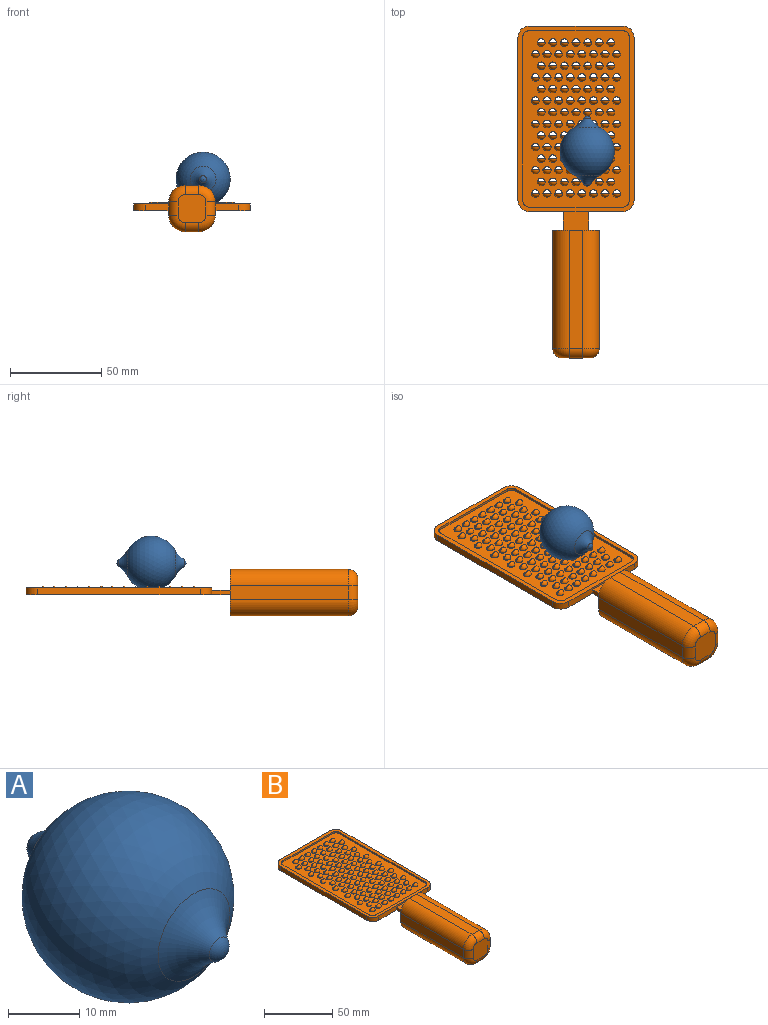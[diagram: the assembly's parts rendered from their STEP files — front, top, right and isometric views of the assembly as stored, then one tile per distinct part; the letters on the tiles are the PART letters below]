
ASSEMBLY  parts=2 mates=1
PART A: 5 faces, bbox 29.7x49.9x29.7 mm
  f0: sphere r=14.84mm, area 2431.8mm2, adj f1,f4
  f1: torus R=13.59mm, axis (0,-1,0), area 195.4mm2, adj f0,f2
  f2: sphere r=2.29mm, area 15.1mm2, adj f1
  f3: sphere r=2.29mm, area 15.1mm2, adj f4
  f4: torus R=13.59mm, axis (0,-1,0), area 195.4mm2, adj f0,f3
PART B: 462 faces, bbox 63.5x181.6x25.4 mm
  f0: plane 96.55x58.45mm, normal (0,0,1), area 4213mm2, adj f11,f12,f13,f14,f15,f16,f17,f18
  f1: plane 50.8x3.81mm, normal (0,-1,0), area 158.1mm2, adj f2,f4,f5,f10,f124,f125,f126
  f2: plane 101.6x63.5mm, normal (0,0,1), area 790.7mm2, adj f1,f3,f4,f5,f6,f7,f8,f9
  f3: plane 88.9x3.81mm, normal (-1,0,0), area 338.7mm2, adj f2,f4,f9,f10
  f4: cylinder r=6.35mm len=6.35mm, axis (0,0,-1), area 38mm2, adj f1,f2,f3,f10
  f5: cylinder r=6.35mm len=6.35mm, axis (0,0,-1), area 38mm2, adj f1,f2,f6,f10
  f6: plane 88.9x3.81mm, normal (1,0,0), area 338.7mm2, adj f2,f5,f7,f10
  f7: cylinder r=6.35mm len=6.35mm, axis (0,0,-1), area 38mm2, adj f2,f6,f8,f10
  f8: plane 50.8x3.81mm, normal (0,1,0), area 193.5mm2, adj f2,f7,f9,f10
  f9: cylinder r=6.35mm len=6.35mm, axis (0,0,-1), area 38mm2, adj f2,f3,f8,f10
  f10: plane 111.76x63.5mm, normal (0,0,-1), area 5361.8mm2, adj f1,f3,f4,f5,f6,f7,f8,f9
  f11: plane 88.9x1.27mm, normal (1,0,0), area 112.9mm2, adj f0,f2,f12,f18
  f12: cylinder r=3.81mm len=3.81mm, axis (0,0,-1), area 7.6mm2, adj f0,f2,f11,f13
  f13: plane 50.8x1.27mm, normal (0,1,0), area 64.5mm2, adj f0,f2,f12,f14
  f14: cylinder r=3.81mm len=3.81mm, axis (0,0,-1), area 7.6mm2, adj f0,f2,f13,f15
  f15: plane 88.9x1.27mm, normal (-1,0,0), area 112.9mm2, adj f0,f2,f14,f16
  f16: cylinder r=3.81mm len=3.81mm, axis (0,0,-1), area 7.6mm2, adj f0,f2,f15,f17
  f17: plane 50.8x1.27mm, normal (0,-1,0), area 64.5mm2, adj f0,f2,f16,f18
  f18: cylinder r=3.81mm len=3.81mm, axis (0,0,-1), area 7.6mm2, adj f0,f2,f11,f17
  f19: cylinder r=1.91mm len=3.81mm, axis (0,0,1), area 30.4mm2, adj f0,f10,f166
  f20: cylinder r=1.91mm len=3.81mm, axis (0,0,1), area 30.4mm2, adj f0,f10,f430
  f21: cylinder r=1.91mm len=3.81mm, axis (0,0,1), area 30.4mm2, adj f0,f10,f206
  f22: cylinder r=1.91mm len=3.81mm, axis (0,0,1), area 30.4mm2, adj f0,f10,f274,f275,f278
  f23: cylinder r=1.91mm len=3.81mm, axis (0,0,1), area 30.4mm2, adj f0,f10,f297
  f24: cylinder r=1.91mm len=3.81mm, axis (0,0,1), area 30.4mm2, adj f0,f10,f385
  f25: cylinder r=1.91mm len=3.81mm, axis (0,0,1), area 30.4mm2, adj f0,f10,f339
  f26: cylinder r=1.91mm len=3.81mm, axis (0,0,1), area 30.4mm2, adj f0,f10,f294
  f27: cylinder r=1.91mm len=3.81mm, axis (0,0,1), area 30.4mm2, adj f0,f10,f247
  f28: cylinder r=1.91mm len=3.81mm, axis (0,0,1), area 30.4mm2, adj f0,f10,f391
  f29: cylinder r=1.91mm len=3.81mm, axis (0,0,1), area 30.4mm2, adj f0,f10,f345
  f30: cylinder r=1.91mm len=3.81mm, axis (0,0,1), area 30.4mm2, adj f0,f10,f300
  f31: cylinder r=1.91mm len=3.81mm, axis (0,0,1), area 30.4mm2, adj f0,f10,f268
  f32: cylinder r=1.91mm len=3.81mm, axis (0,0,1), area 30.4mm2, adj f0,f10,f342
  f33: cylinder r=1.91mm len=3.81mm, axis (0,0,1), area 30.4mm2, adj f0,f10,f388
  f34: cylinder r=1.91mm len=3.81mm, axis (0,0,1), area 30.4mm2, adj f0,f10,f433
  f35: cylinder r=1.91mm len=3.81mm, axis (0,0,1), area 30.4mm2, adj f0,f10,f208
  f36: cylinder r=1.91mm len=3.81mm, axis (0,0,1), area 30.4mm2, adj f0,f10,f379
  f37: cylinder r=1.91mm len=3.81mm, axis (0,0,1), area 30.4mm2, adj f0,f10,f333
  f38: cylinder r=1.91mm len=3.81mm, axis (0,0,1), area 30.4mm2, adj f0,f10,f288
  f39: cylinder r=1.91mm len=3.81mm, axis (0,0,1), area 30.4mm2, adj f0,f10,f241
  f40: cylinder r=1.91mm len=3.81mm, axis (0,0,1), area 30.4mm2, adj f0,f10,f331
  f41: cylinder r=1.91mm len=3.81mm, axis (0,0,1), area 30.4mm2, adj f0,f10,f376
  f42: cylinder r=1.91mm len=3.81mm, axis (0,0,1), area 30.4mm2, adj f0,f10,f421
  f43: cylinder r=1.91mm len=3.81mm, axis (0,0,1), area 30.4mm2, adj f0,f10,f196
  f44: cylinder r=1.91mm len=3.81mm, axis (0,0,1), area 30.4mm2, adj f0,f10,f336
  f45: cylinder r=1.91mm len=3.81mm, axis (0,0,1), area 30.4mm2, adj f0,f10,f382
  f46: cylinder r=1.91mm len=3.81mm, axis (0,0,1), area 30.4mm2, adj f0,f10,f427
  f47: cylinder r=1.91mm len=3.81mm, axis (0,0,1), area 30.4mm2, adj f0,f10,f203
  f48: cylinder r=1.91mm len=3.81mm, axis (0,0,1), area 30.4mm2, adj f0,f10,f424
  f49: cylinder r=1.91mm len=3.81mm, axis (0,0,1), area 30.4mm2, adj f0,f10,f199
  f50: cylinder r=1.91mm len=3.81mm, axis (0,0,1), area 30.4mm2, adj f0,f10,f244
  f51: cylinder r=1.91mm len=3.81mm, axis (0,0,1), area 30.4mm2, adj f0,f10,f291
  f52: cylinder r=1.91mm len=3.81mm, axis (0,0,1), area 30.4mm2, adj f0,f10,f154
  f53: cylinder r=1.91mm len=3.81mm, axis (0,0,1), area 30.4mm2, adj f0,f10,f160
  f54: cylinder r=1.91mm len=3.81mm, axis (0,0,1), area 30.4mm2, adj f0,f10,f163
  f55: cylinder r=1.91mm len=3.81mm, axis (0,0,1), area 30.4mm2, adj f0,f10,f157
  f56: cylinder r=1.91mm len=3.81mm, axis (0,0,1), area 30.4mm2, adj f0,f10,f436
  f57: cylinder r=1.91mm len=3.81mm, axis (0,0,1), area 30.4mm2, adj f0,f10,f145
  f58: cylinder r=1.91mm len=3.81mm, axis (0,0,1), area 30.4mm2, adj f0,f10,f148
  f59: cylinder r=1.91mm len=3.81mm, axis (0,0,1), area 30.4mm2, adj f0,f10,f151
  f60: cylinder r=1.91mm len=3.81mm, axis (0,0,1), area 30.4mm2, adj f0,f10,f309
  f61: cylinder r=1.91mm len=3.81mm, axis (0,0,1), area 30.4mm2, adj f0,f10,f355
  f62: cylinder r=1.91mm len=3.81mm, axis (0,0,1), area 30.4mm2, adj f0,f10,f400
  f63: cylinder r=1.91mm len=3.81mm, axis (0,0,1), area 30.4mm2, adj f0,f10,f445
  f64: cylinder r=1.91mm len=3.81mm, axis (0,0,1), area 30.4mm2, adj f0,f10,f175
  f65: cylinder r=1.91mm len=3.81mm, axis (0,0,1), area 30.4mm2, adj f0,f10,f220
  f66: cylinder r=1.91mm len=3.81mm, axis (0,0,1), area 30.4mm2, adj f0,f10,f259
  f67: cylinder r=1.91mm len=3.81mm, axis (0,0,1), area 30.4mm2, adj f0,f10,f312
  f68: cylinder r=1.91mm len=3.81mm, axis (0,0,1), area 30.4mm2, adj f0,f10,f361
  f69: cylinder r=1.91mm len=3.81mm, axis (0,0,1), area 30.4mm2, adj f0,f10,f315
  f70: cylinder r=1.91mm len=3.81mm, axis (0,0,1), area 30.4mm2, adj f0,f10,f262
  f71: cylinder r=1.91mm len=3.81mm, axis (0,0,1), area 30.4mm2, adj f0,f10,f223
  f72: cylinder r=1.91mm len=3.81mm, axis (0,0,1), area 30.4mm2, adj f0,f10,f358
  f73: cylinder r=1.91mm len=3.81mm, axis (0,0,1), area 30.4mm2, adj f0,f10,f403
  f74: cylinder r=1.91mm len=3.81mm, axis (0,0,1), area 30.4mm2, adj f0,f10,f448
  f75: cylinder r=1.91mm len=3.81mm, axis (0,0,1), area 30.4mm2, adj f0,f10,f178
  f76: cylinder r=1.91mm len=3.81mm, axis (0,0,1), area 30.4mm2, adj f0,f10,f214
  f77: cylinder r=1.91mm len=3.81mm, axis (0,0,1), area 30.4mm2, adj f0,f10,f169
  f78: cylinder r=1.91mm len=3.81mm, axis (0,0,1), area 30.4mm2, adj f0,f10,f439
  f79: cylinder r=1.91mm len=3.81mm, axis (0,0,1), area 30.4mm2, adj f0,f10,f394
  f80: cylinder r=1.91mm len=3.81mm, axis (0,0,1), area 30.4mm2, adj f0,f10,f348
  f81: cylinder r=1.91mm len=3.81mm, axis (0,0,1), area 30.4mm2, adj f0,f10,f303
  f82: cylinder r=1.91mm len=3.81mm, axis (0,0,1), area 30.4mm2, adj f0,f10,f250
  f83: cylinder r=1.91mm len=3.81mm, axis (0,0,1), area 30.4mm2, adj f0,f10,f212
  f84: cylinder r=1.91mm len=3.81mm, axis (0,0,1), area 30.4mm2, adj f0,f10,f442
  f85: cylinder r=1.91mm len=3.81mm, axis (0,0,1), area 30.4mm2, adj f0,f10,f172
  f86: cylinder r=1.91mm len=3.81mm, axis (0,0,1), area 30.4mm2, adj f0,f10,f217
  f87: cylinder r=1.91mm len=3.81mm, axis (0,0,1), area 30.4mm2, adj f0,f10,f256
  f88: cylinder r=1.91mm len=3.81mm, axis (0,0,1), area 30.4mm2, adj f0,f10,f397
  f89: cylinder r=1.91mm len=3.81mm, axis (0,0,1), area 30.4mm2, adj f0,f10,f352
  f90: cylinder r=1.91mm len=3.81mm, axis (0,0,1), area 30.4mm2, adj f0,f10,f306
  f91: cylinder r=1.91mm len=3.81mm, axis (0,0,1), area 30.4mm2, adj f0,f10,f253
  f92: cylinder r=1.91mm len=3.81mm, axis (0,0,1), area 30.4mm2, adj f0,f10,f370
  f93: cylinder r=1.91mm len=3.81mm, axis (0,0,1), area 30.4mm2, adj f0,f10,f415
  f94: cylinder r=1.91mm len=3.81mm, axis (0,0,1), area 30.4mm2, adj f0,f10,f460
  f95: cylinder r=1.91mm len=3.81mm, axis (0,0,1), area 30.4mm2, adj f0,f10,f190
  f96: cylinder r=1.91mm len=3.81mm, axis (0,0,1), area 30.4mm2, adj f0,f10,f324
  f97: cylinder r=1.91mm len=3.81mm, axis (0,0,1), area 30.4mm2, adj f0,f10,f279
  f98: cylinder r=1.91mm len=3.81mm, axis (0,0,1), area 30.4mm2, adj f0,f10,f233
  f99: cylinder r=1.91mm len=3.81mm, axis (0,0,1), area 30.4mm2, adj f0,f10,f187
  f100: cylinder r=1.91mm len=3.81mm, axis (0,0,1), area 30.4mm2, adj f0,f10,f418
  f101: cylinder r=1.91mm len=3.81mm, axis (0,0,1), area 30.4mm2, adj f0,f10,f193
  f102: cylinder r=1.91mm len=3.81mm, axis (0,0,1), area 30.4mm2, adj f0,f10,f238
  f103: cylinder r=1.91mm len=3.81mm, axis (0,0,1), area 30.4mm2, adj f0,f10,f285
  f104: cylinder r=1.91mm len=3.81mm, axis (0,0,1), area 30.4mm2, adj f0,f10,f372
  f105: cylinder r=1.91mm len=3.81mm, axis (0,0,1), area 30.4mm2, adj f0,f10,f327
  f106: cylinder r=1.91mm len=3.81mm, axis (0,0,1), area 30.4mm2, adj f0,f10,f282
  f107: cylinder r=1.91mm len=3.81mm, axis (0,0,1), area 30.4mm2, adj f0,f10,f235
  f108: cylinder r=1.91mm len=3.81mm, axis (0,0,1), area 30.4mm2, adj f0,f10,f409
  f109: cylinder r=1.91mm len=3.81mm, axis (0,0,1), area 30.4mm2, adj f0,f10,f364
  f110: cylinder r=1.91mm len=3.81mm, axis (0,0,1), area 30.4mm2, adj f0,f10,f320
  f111: cylinder r=1.91mm len=3.81mm, axis (0,0,1), area 30.4mm2, adj f0,f10,f265
  f112: cylinder r=1.91mm len=3.81mm, axis (0,0,1), area 30.4mm2, adj f0,f10,f226
  f113: cylinder r=1.91mm len=3.81mm, axis (0,0,1), area 30.4mm2, adj f0,f10,f181
  f114: cylinder r=1.91mm len=3.81mm, axis (0,0,1), area 30.4mm2, adj f0,f10,f451
  f115: cylinder r=1.91mm len=3.81mm, axis (0,0,1), area 30.4mm2, adj f0,f10,f406
  f116: cylinder r=1.91mm len=3.81mm, axis (0,0,1), area 30.4mm2, adj f0,f10,f457
  f117: cylinder r=1.91mm len=3.81mm, axis (0,0,1), area 30.4mm2, adj f0,f10,f412
  f118: cylinder r=1.91mm len=3.81mm, axis (0,0,1), area 30.4mm2, adj f0,f10,f367
  f119: cylinder r=1.91mm len=3.81mm, axis (0,0,1), area 30.4mm2, adj f0,f10,f321
  f120: cylinder r=1.91mm len=3.81mm, axis (0,0,1), area 30.4mm2, adj f0,f10,f454
  f121: cylinder r=1.91mm len=3.81mm, axis (0,0,1), area 30.4mm2, adj f0,f10,f184
  f122: cylinder r=1.91mm len=3.81mm, axis (0,0,1), area 30.4mm2, adj f0,f10,f229
  f123: cylinder r=1.91mm len=3.81mm, axis (0,0,1), area 30.4mm2, adj f0,f10,f271
  f124: plane 10.16x2.54mm, normal (1,0,0), area 25.8mm2, adj f1,f10,f125,f136
  f125: plane 13.97x10.16mm, normal (0,0,1), area 141.9mm2, adj f1,f124,f126,f136
  f126: plane 10.16x2.54mm, normal (-1,0,0), area 25.8mm2, adj f1,f10,f125,f136
  f127: plane 64.77x7.62mm, normal (-1,0,0), area 493.5mm2, adj f128,f134,f136,f141
  f128: cylinder r=8.89mm len=64.77mm, axis (0,1,0), area 904.5mm2, adj f127,f129,f136,f139
  f129: plane 64.77x7.62mm, normal (0,0,-1), area 493.5mm2, adj f128,f130,f136,f137
  f130: cylinder r=8.89mm len=64.77mm, axis (0,1,0), area 904.5mm2, adj f129,f131,f136,f138
  f131: plane 64.77x7.62mm, normal (1,0,0), area 493.5mm2, adj f130,f132,f136,f140
  f132: cylinder r=8.89mm len=64.77mm, axis (0,1,0), area 904.5mm2, adj f131,f133,f136,f142
  f133: plane 64.77x7.62mm, normal (0,0,1), area 493.5mm2, adj f132,f134,f136,f144
  f134: cylinder r=8.89mm len=64.77mm, axis (0,1,0), area 904.5mm2, adj f127,f133,f136,f143
  f135: plane 15.24x15.24mm, normal (0,-1,0), area 219.8mm2, adj f137,f138,f139,f140,f141,f142,f143,f144
  f136: plane 25.4x25.4mm, normal (0,1,0), area 541.8mm2, adj f10,f124,f125,f126,f127,f128,f129,f130
  f137: cylinder r=5.08mm len=7.62mm, axis (-1,0,0), area 60.8mm2, adj f129,f135,f138,f139
  f138: torus R=3.81mm, axis (0,-1,0), area 88.3mm2, adj f130,f135,f137,f140
  f139: torus R=3.81mm, axis (0,-1,0), area 88.3mm2, adj f128,f135,f137,f141
  f140: cylinder r=5.08mm len=7.62mm, axis (0,0,-1), area 60.8mm2, adj f131,f135,f138,f142
  f141: cylinder r=5.08mm len=7.62mm, axis (0,0,1), area 60.8mm2, adj f127,f135,f139,f143
  f142: torus R=3.81mm, axis (0,-1,0), area 88.3mm2, adj f132,f135,f140,f144
  f143: torus R=3.81mm, axis (0,-1,0), area 88.3mm2, adj f134,f135,f141,f144
  f144: cylinder r=5.08mm len=7.62mm, axis (1,0,0), area 60.8mm2, adj f133,f135,f142,f143
  f145: sphere r=1.91mm, area 11.4mm2, adj f57,f146
  f146: plane 4.45x2.22mm, normal (0,1,0), area 2.1mm2, adj f0,f145,f147
  f147: sphere r=2.22mm, area 15.5mm2, adj f0,f146
  f148: sphere r=1.91mm, area 11.4mm2, adj f58,f149
  f149: plane 4.45x2.22mm, normal (0,1,0), area 2.1mm2, adj f0,f148,f150
  f150: sphere r=2.22mm, area 15.5mm2, adj f0,f149
  f151: sphere r=1.91mm, area 11.4mm2, adj f59,f152
  f152: plane 4.45x2.22mm, normal (0,1,0), area 2.1mm2, adj f0,f151,f153
  f153: sphere r=2.22mm, area 15.5mm2, adj f0,f152
  f154: sphere r=1.91mm, area 11.4mm2, adj f52,f155
  f155: plane 4.45x2.22mm, normal (0,1,0), area 2.1mm2, adj f0,f154,f156
  f156: sphere r=2.22mm, area 15.5mm2, adj f0,f155
  f157: sphere r=1.91mm, area 11.4mm2, adj f55,f158
  f158: plane 4.45x2.22mm, normal (0,1,0), area 2.1mm2, adj f0,f157,f159
  f159: sphere r=2.22mm, area 15.5mm2, adj f0,f158
  f160: sphere r=1.91mm, area 11.4mm2, adj f53,f161
  f161: plane 4.45x2.22mm, normal (0,1,0), area 2.1mm2, adj f0,f160,f162
  f162: sphere r=2.22mm, area 15.5mm2, adj f0,f161
  f163: sphere r=1.91mm, area 11.4mm2, adj f54,f164
  f164: plane 4.45x2.22mm, normal (0,1,0), area 2.1mm2, adj f0,f163,f165
  f165: sphere r=2.22mm, area 15.5mm2, adj f0,f164
  f166: sphere r=1.91mm, area 11.4mm2, adj f19,f167
  f167: plane 4.45x2.22mm, normal (0,1,0), area 2.1mm2, adj f0,f166,f168
  f168: sphere r=2.22mm, area 15.5mm2, adj f0,f167
  f169: sphere r=1.91mm, area 11.4mm2, adj f77,f170
  f170: plane 4.45x2.22mm, normal (0,1,0), area 2.1mm2, adj f0,f169,f171
  f171: sphere r=2.22mm, area 15.5mm2, adj f0,f170
  f172: sphere r=1.91mm, area 11.4mm2, adj f85,f173
  f173: plane 4.45x2.22mm, normal (0,1,0), area 2.1mm2, adj f0,f172,f174
  f174: sphere r=2.22mm, area 15.5mm2, adj f0,f173
  f175: sphere r=1.91mm, area 11.4mm2, adj f64,f176
  f176: plane 4.45x2.22mm, normal (0,1,0), area 2.1mm2, adj f0,f175,f177
  f177: sphere r=2.22mm, area 15.5mm2, adj f0,f176
  f178: sphere r=1.91mm, area 11.4mm2, adj f75,f179
  f179: plane 4.45x2.22mm, normal (0,1,0), area 2.1mm2, adj f0,f178,f180
  f180: sphere r=2.22mm, area 15.5mm2, adj f0,f179
  f181: sphere r=1.91mm, area 11.4mm2, adj f113,f182
  f182: plane 4.45x2.22mm, normal (0,1,0), area 2.1mm2, adj f0,f181,f183
  f183: sphere r=2.22mm, area 15.5mm2, adj f0,f182
  f184: sphere r=1.91mm, area 11.4mm2, adj f121,f185
  f185: plane 4.45x2.22mm, normal (0,1,0), area 2.1mm2, adj f0,f184,f186
  f186: sphere r=2.22mm, area 15.5mm2, adj f0,f185
  f187: sphere r=1.91mm, area 11.4mm2, adj f99,f188
  f188: plane 4.45x2.22mm, normal (0,1,0), area 2.1mm2, adj f0,f187,f189
  f189: sphere r=2.22mm, area 15.5mm2, adj f0,f188
  f190: sphere r=1.91mm, area 11.4mm2, adj f95,f191
  f191: plane 4.45x2.22mm, normal (0,1,0), area 2.1mm2, adj f0,f190,f192
  f192: sphere r=2.22mm, area 15.5mm2, adj f0,f191
  f193: sphere r=1.91mm, area 11.4mm2, adj f101,f194
  f194: plane 4.45x2.22mm, normal (0,1,0), area 2.1mm2, adj f0,f193,f195
  f195: sphere r=2.22mm, area 15.5mm2, adj f0,f194
  f196: sphere r=1.91mm, area 11.4mm2, adj f43,f198
  f197: sphere r=2.22mm, area 15.5mm2, adj f0,f198
  f198: plane 4.45x2.22mm, normal (0,1,0), area 2.1mm2, adj f0,f196,f197
  f199: sphere r=1.91mm, area 11.4mm2, adj f49,f201
  f200: sphere r=2.22mm, area 15.5mm2, adj f0,f201
  f201: plane 4.45x2.22mm, normal (0,1,0), area 2.1mm2, adj f0,f199,f200
  f202: plane 4.45x2.22mm, normal (0,1,0), area 2.1mm2, adj f0,f203,f204
  f203: sphere r=1.91mm, area 11.4mm2, adj f47,f202
  f204: sphere r=2.22mm, area 15.5mm2, adj f0,f202
  f205: plane 4.45x2.22mm, normal (0,1,0), area 2.1mm2, adj f0,f206,f207
  f206: sphere r=1.91mm, area 11.4mm2, adj f21,f205
  f207: sphere r=2.22mm, area 15.5mm2, adj f0,f205
  f208: sphere r=1.91mm, area 11.4mm2, adj f35,f210
  f209: sphere r=2.22mm, area 15.5mm2, adj f0,f210
  f210: plane 4.45x2.22mm, normal (0,1,0), area 2.1mm2, adj f0,f208,f209
  f211: plane 4.45x2.22mm, normal (0,1,0), area 2.1mm2, adj f0,f212,f213
  f212: sphere r=1.91mm, area 11.4mm2, adj f83,f211
  f213: sphere r=2.22mm, area 15.5mm2, adj f0,f211
  f214: sphere r=1.91mm, area 11.4mm2, adj f76,f216
  f215: sphere r=2.22mm, area 15.5mm2, adj f0,f216
  f216: plane 4.45x2.22mm, normal (0,1,0), area 2.1mm2, adj f0,f214,f215
  f217: sphere r=1.91mm, area 11.4mm2, adj f86,f219
  f218: sphere r=2.22mm, area 15.5mm2, adj f0,f219
  f219: plane 4.45x2.22mm, normal (0,1,0), area 2.1mm2, adj f0,f217,f218
  f220: sphere r=1.91mm, area 11.4mm2, adj f65,f222
  f221: sphere r=2.22mm, area 15.5mm2, adj f0,f222
  f222: plane 4.45x2.22mm, normal (0,1,0), area 2.1mm2, adj f0,f220,f221
  f223: sphere r=1.91mm, area 11.4mm2, adj f71,f225
  f224: sphere r=2.22mm, area 15.5mm2, adj f0,f225
  f225: plane 4.45x2.22mm, normal (0,1,0), area 2.1mm2, adj f0,f223,f224
  f226: sphere r=1.91mm, area 11.4mm2, adj f112,f228
  f227: sphere r=2.22mm, area 15.5mm2, adj f0,f228
  f228: plane 4.45x2.22mm, normal (0,1,0), area 2.1mm2, adj f0,f226,f227
  f229: sphere r=1.91mm, area 11.4mm2, adj f122,f231
  f230: sphere r=2.22mm, area 15.5mm2, adj f0,f231
  f231: plane 4.45x2.22mm, normal (0,1,0), area 2.1mm2, adj f0,f229,f230
  f232: plane 4.45x2.22mm, normal (0,1,0), area 2.1mm2, adj f0,f233,f234
  f233: sphere r=1.91mm, area 11.4mm2, adj f98,f232
  f234: sphere r=2.22mm, area 15.5mm2, adj f0,f232
  f235: sphere r=1.91mm, area 11.4mm2, adj f107,f237
  f236: sphere r=2.22mm, area 15.5mm2, adj f0,f237
  f237: plane 4.45x2.22mm, normal (0,1,0), area 2.1mm2, adj f0,f235,f236
  f238: sphere r=1.91mm, area 11.4mm2, adj f102,f240
  f239: sphere r=2.22mm, area 15.5mm2, adj f0,f240
  f240: plane 4.45x2.22mm, normal (0,1,0), area 2.1mm2, adj f0,f238,f239
  f241: sphere r=1.91mm, area 11.4mm2, adj f39,f243
  f242: sphere r=2.22mm, area 15.5mm2, adj f0,f243
  f243: plane 4.45x2.22mm, normal (0,1,0), area 2.1mm2, adj f0,f241,f242
  f244: sphere r=1.91mm, area 11.4mm2, adj f50,f246
  f245: sphere r=2.22mm, area 15.5mm2, adj f0,f246
  f246: plane 4.45x2.22mm, normal (0,1,0), area 2.1mm2, adj f0,f244,f245
  f247: sphere r=1.91mm, area 11.4mm2, adj f27,f249
  f248: sphere r=2.22mm, area 15.5mm2, adj f0,f249
  f249: plane 4.45x2.22mm, normal (0,1,0), area 2.1mm2, adj f0,f247,f248
  f250: sphere r=1.91mm, area 11.4mm2, adj f82,f252
  f251: sphere r=2.22mm, area 15.5mm2, adj f0,f252
  f252: plane 4.45x2.22mm, normal (0,1,0), area 2.1mm2, adj f0,f250,f251
  f253: sphere r=1.91mm, area 11.4mm2, adj f91,f255
  f254: sphere r=2.22mm, area 15.5mm2, adj f0,f255
  f255: plane 4.45x2.22mm, normal (0,1,0), area 2.1mm2, adj f0,f253,f254
  f256: sphere r=1.91mm, area 11.4mm2, adj f87,f258
  f257: sphere r=2.22mm, area 15.5mm2, adj f0,f258
  f258: plane 4.45x2.22mm, normal (0,1,0), area 2.1mm2, adj f0,f256,f257
  f259: sphere r=1.91mm, area 11.4mm2, adj f66,f261
  f260: sphere r=2.22mm, area 15.5mm2, adj f0,f261
  f261: plane 4.45x2.22mm, normal (0,1,0), area 2.1mm2, adj f0,f259,f260
  f262: sphere r=1.91mm, area 11.4mm2, adj f70,f264
  f263: sphere r=2.22mm, area 15.5mm2, adj f0,f264
  f264: plane 4.45x2.22mm, normal (0,1,0), area 2.1mm2, adj f0,f262,f263
  f265: sphere r=1.91mm, area 11.4mm2, adj f111,f267
  f266: sphere r=2.22mm, area 15.5mm2, adj f0,f267
  f267: plane 4.45x2.22mm, normal (0,1,0), area 2.1mm2, adj f0,f265,f266
  f268: sphere r=1.91mm, area 11.4mm2, adj f31,f270
  f269: sphere r=2.22mm, area 15.5mm2, adj f0,f270
  f270: plane 4.45x2.22mm, normal (0,1,0), area 2.1mm2, adj f0,f268,f269
  f271: sphere r=1.91mm, area 11.4mm2, adj f123,f273
  f272: sphere r=2.22mm, area 15.5mm2, adj f0,f273
  f273: plane 4.45x2.22mm, normal (0,1,0), area 2.1mm2, adj f0,f271,f272
  f274: plane 3.81x1.91mm, normal (0,0,-1), area 0mm2, adj f22,f275
  f275: sphere r=1.91mm, area 11.4mm2, adj f22,f274,f278
  f276: sphere r=2.22mm, area 15.5mm2, adj f0,f277
  f277: plane 4.45x2.22mm, normal (0,1,0), area 2.1mm2, adj f0,f276,f278
  f278: sphere r=1.91mm, area 0mm2, adj f22,f275,f277
  f279: sphere r=1.91mm, area 11.4mm2, adj f97,f281
  f280: sphere r=2.22mm, area 15.5mm2, adj f0,f281
  f281: plane 4.45x2.22mm, normal (0,1,0), area 2.1mm2, adj f0,f279,f280
  f282: sphere r=1.91mm, area 11.4mm2, adj f106,f284
  f283: sphere r=2.22mm, area 15.5mm2, adj f0,f284
  f284: plane 4.45x2.22mm, normal (0,1,0), area 2.1mm2, adj f0,f282,f283
  f285: sphere r=1.91mm, area 11.4mm2, adj f103,f287
  f286: sphere r=2.22mm, area 15.5mm2, adj f0,f287
  f287: plane 4.45x2.22mm, normal (0,1,0), area 2.1mm2, adj f0,f285,f286
  f288: sphere r=1.91mm, area 11.4mm2, adj f38,f290
  f289: sphere r=2.22mm, area 15.5mm2, adj f0,f290
  f290: plane 4.45x2.22mm, normal (0,1,0), area 2.1mm2, adj f0,f288,f289
  f291: sphere r=1.91mm, area 11.4mm2, adj f51,f293
  f292: sphere r=2.22mm, area 15.5mm2, adj f0,f293
  f293: plane 4.45x2.22mm, normal (0,1,0), area 2.1mm2, adj f0,f291,f292
  f294: sphere r=1.91mm, area 11.4mm2, adj f26,f296
  f295: sphere r=2.22mm, area 15.5mm2, adj f0,f296
  f296: plane 4.45x2.22mm, normal (0,1,0), area 2.1mm2, adj f0,f294,f295
  f297: sphere r=1.91mm, area 11.4mm2, adj f23,f299
  f298: sphere r=2.22mm, area 15.5mm2, adj f0,f299
  f299: plane 4.45x2.22mm, normal (0,1,0), area 2.1mm2, adj f0,f297,f298
  f300: sphere r=1.91mm, area 11.4mm2, adj f30,f302
  f301: sphere r=2.22mm, area 15.5mm2, adj f0,f302
  f302: plane 4.45x2.22mm, normal (0,1,0), area 2.1mm2, adj f0,f300,f301
  f303: sphere r=1.91mm, area 11.4mm2, adj f81,f305
  f304: sphere r=2.22mm, area 15.5mm2, adj f0,f305
  f305: plane 4.45x2.22mm, normal (0,1,0), area 2.1mm2, adj f0,f303,f304
  f306: sphere r=1.91mm, area 11.4mm2, adj f90,f308
  f307: sphere r=2.22mm, area 15.5mm2, adj f0,f308
  f308: plane 4.45x2.22mm, normal (0,1,0), area 2.1mm2, adj f0,f306,f307
  f309: sphere r=1.91mm, area 11.4mm2, adj f60,f311
  f310: sphere r=2.22mm, area 15.5mm2, adj f0,f311
  f311: plane 4.45x2.22mm, normal (0,1,0), area 2.1mm2, adj f0,f309,f310
  f312: sphere r=1.91mm, area 11.4mm2, adj f67,f314
  f313: sphere r=2.22mm, area 15.5mm2, adj f0,f314
  f314: plane 4.45x2.22mm, normal (0,1,0), area 2.1mm2, adj f0,f312,f313
  f315: sphere r=1.91mm, area 11.4mm2, adj f69,f317
  f316: sphere r=2.22mm, area 15.5mm2, adj f0,f317
  f317: plane 4.45x2.22mm, normal (0,1,0), area 2.1mm2, adj f0,f315,f316
  f318: sphere r=2.22mm, area 15.5mm2, adj f0,f319
  f319: plane 4.45x2.22mm, normal (0,1,0), area 2.1mm2, adj f0,f318,f320
  f320: sphere r=1.91mm, area 11.4mm2, adj f110,f319
  f321: sphere r=1.91mm, area 11.4mm2, adj f119,f323
  f322: sphere r=2.22mm, area 15.5mm2, adj f0,f323
  f323: plane 4.45x2.22mm, normal (0,1,0), area 2.1mm2, adj f0,f321,f322
  f324: sphere r=1.91mm, area 11.4mm2, adj f96,f326
  f325: sphere r=2.22mm, area 15.5mm2, adj f0,f326
  f326: plane 4.45x2.22mm, normal (0,1,0), area 2.1mm2, adj f0,f324,f325
  f327: sphere r=1.91mm, area 11.4mm2, adj f105,f329
  f328: sphere r=2.22mm, area 15.5mm2, adj f0,f329
  f329: plane 4.45x2.22mm, normal (0,1,0), area 2.1mm2, adj f0,f327,f328
  f330: plane 4.45x2.22mm, normal (0,1,0), area 2.1mm2, adj f0,f331,f332
  f331: sphere r=1.91mm, area 11.4mm2, adj f40,f330
  f332: sphere r=2.22mm, area 15.5mm2, adj f0,f330
  f333: sphere r=1.91mm, area 11.4mm2, adj f37,f335
  f334: sphere r=2.22mm, area 15.5mm2, adj f0,f335
  f335: plane 4.45x2.22mm, normal (0,1,0), area 2.1mm2, adj f0,f333,f334
  f336: sphere r=1.91mm, area 11.4mm2, adj f44,f338
  f337: sphere r=2.22mm, area 15.5mm2, adj f0,f338
  f338: plane 4.45x2.22mm, normal (0,1,0), area 2.1mm2, adj f0,f336,f337
  f339: sphere r=1.91mm, area 11.4mm2, adj f25,f341
  f340: sphere r=2.22mm, area 15.5mm2, adj f0,f341
  f341: plane 4.45x2.22mm, normal (0,1,0), area 2.1mm2, adj f0,f339,f340
  f342: sphere r=1.91mm, area 11.4mm2, adj f32,f344
  f343: sphere r=2.22mm, area 15.5mm2, adj f0,f344
  f344: plane 4.45x2.22mm, normal (0,1,0), area 2.1mm2, adj f0,f342,f343
  f345: sphere r=1.91mm, area 11.4mm2, adj f29,f347
  f346: sphere r=2.22mm, area 15.5mm2, adj f0,f347
  f347: plane 4.45x2.22mm, normal (0,1,0), area 2.1mm2, adj f0,f345,f346
  f348: sphere r=1.91mm, area 11.4mm2, adj f80,f350
  f349: sphere r=2.22mm, area 15.5mm2, adj f0,f350
  f350: plane 4.45x2.22mm, normal (0,1,0), area 2.1mm2, adj f0,f348,f349
  f351: plane 4.45x2.22mm, normal (0,1,0), area 2.1mm2, adj f0,f352,f353
  f352: sphere r=1.91mm, area 11.4mm2, adj f89,f351
  f353: sphere r=2.22mm, area 15.5mm2, adj f0,f351
  f354: plane 4.45x2.22mm, normal (0,1,0), area 2.1mm2, adj f0,f355,f356
  f355: sphere r=1.91mm, area 11.4mm2, adj f61,f354
  f356: sphere r=2.22mm, area 15.5mm2, adj f0,f354
  f357: plane 4.45x2.22mm, normal (0,1,0), area 2.1mm2, adj f0,f358,f359
  f358: sphere r=1.91mm, area 11.4mm2, adj f72,f357
  f359: sphere r=2.22mm, area 15.5mm2, adj f0,f357
  f360: plane 4.45x2.22mm, normal (0,1,0), area 2.1mm2, adj f0,f361,f362
  f361: sphere r=1.91mm, area 11.4mm2, adj f68,f360
  f362: sphere r=2.22mm, area 15.5mm2, adj f0,f360
  f363: plane 4.45x2.22mm, normal (0,1,0), area 2.1mm2, adj f0,f364,f365
  f364: sphere r=1.91mm, area 11.4mm2, adj f109,f363
  f365: sphere r=2.22mm, area 15.5mm2, adj f0,f363
  f366: plane 4.45x2.22mm, normal (0,1,0), area 2.1mm2, adj f0,f367,f368
  f367: sphere r=1.91mm, area 11.4mm2, adj f118,f366
  f368: sphere r=2.22mm, area 15.5mm2, adj f0,f366
  f369: plane 4.45x2.22mm, normal (0,1,0), area 2.1mm2, adj f0,f370,f371
  f370: sphere r=1.91mm, area 11.4mm2, adj f92,f369
  f371: sphere r=2.22mm, area 15.5mm2, adj f0,f369
  f372: sphere r=1.91mm, area 11.4mm2, adj f104,f374
  f373: sphere r=2.22mm, area 15.5mm2, adj f0,f374
  f374: plane 4.45x2.22mm, normal (0,1,0), area 2.1mm2, adj f0,f372,f373
  f375: plane 4.45x2.22mm, normal (0,1,0), area 2.1mm2, adj f0,f376,f377
  f376: sphere r=1.91mm, area 11.4mm2, adj f41,f375
  f377: sphere r=2.22mm, area 15.5mm2, adj f0,f375
  f378: plane 4.45x2.22mm, normal (0,1,0), area 2.1mm2, adj f0,f379,f380
  f379: sphere r=1.91mm, area 11.4mm2, adj f36,f378
  f380: sphere r=2.22mm, area 15.5mm2, adj f0,f378
  f381: plane 4.45x2.22mm, normal (0,1,0), area 2.1mm2, adj f0,f382,f383
  f382: sphere r=1.91mm, area 11.4mm2, adj f45,f381
  f383: sphere r=2.22mm, area 15.5mm2, adj f0,f381
  f384: plane 4.45x2.22mm, normal (0,1,0), area 2.1mm2, adj f0,f385,f386
  f385: sphere r=1.91mm, area 11.4mm2, adj f24,f384
  f386: sphere r=2.22mm, area 15.5mm2, adj f0,f384
  f387: plane 4.45x2.22mm, normal (0,1,0), area 2.1mm2, adj f0,f388,f389
  f388: sphere r=1.91mm, area 11.4mm2, adj f33,f387
  f389: sphere r=2.22mm, area 15.5mm2, adj f0,f387
  f390: plane 4.45x2.22mm, normal (0,1,0), area 2.1mm2, adj f0,f391,f392
  f391: sphere r=1.91mm, area 11.4mm2, adj f28,f390
  f392: sphere r=2.22mm, area 15.5mm2, adj f0,f390
  f393: plane 4.45x2.22mm, normal (0,1,0), area 2.1mm2, adj f0,f394,f395
  f394: sphere r=1.91mm, area 11.4mm2, adj f79,f393
  f395: sphere r=2.22mm, area 15.5mm2, adj f0,f393
  f396: plane 4.45x2.22mm, normal (0,1,0), area 2.1mm2, adj f0,f397,f398
  f397: sphere r=1.91mm, area 11.4mm2, adj f88,f396
  f398: sphere r=2.22mm, area 15.5mm2, adj f0,f396
  f399: plane 4.45x2.22mm, normal (0,1,0), area 2.1mm2, adj f0,f400,f401
  f400: sphere r=1.91mm, area 11.4mm2, adj f62,f399
  f401: sphere r=2.22mm, area 15.5mm2, adj f0,f399
  f402: plane 4.45x2.22mm, normal (0,1,0), area 2.1mm2, adj f0,f403,f404
  f403: sphere r=1.91mm, area 11.4mm2, adj f73,f402
  f404: sphere r=2.22mm, area 15.5mm2, adj f0,f402
  f405: plane 4.45x2.22mm, normal (0,1,0), area 2.1mm2, adj f0,f406,f407
  f406: sphere r=1.91mm, area 11.4mm2, adj f115,f405
  f407: sphere r=2.22mm, area 15.5mm2, adj f0,f405
  f408: plane 4.45x2.22mm, normal (0,1,0), area 2.1mm2, adj f0,f409,f410
  f409: sphere r=1.91mm, area 11.4mm2, adj f108,f408
  f410: sphere r=2.22mm, area 15.5mm2, adj f0,f408
  f411: plane 4.45x2.22mm, normal (0,1,0), area 2.1mm2, adj f0,f412,f413
  f412: sphere r=1.91mm, area 11.4mm2, adj f117,f411
  f413: sphere r=2.22mm, area 15.5mm2, adj f0,f411
  f414: plane 4.45x2.22mm, normal (0,1,0), area 2.1mm2, adj f0,f415,f416
  f415: sphere r=1.91mm, area 11.4mm2, adj f93,f414
  f416: sphere r=2.22mm, area 15.5mm2, adj f0,f414
  f417: plane 4.45x2.22mm, normal (0,1,0), area 2.1mm2, adj f0,f418,f419
  f418: sphere r=1.91mm, area 11.4mm2, adj f100,f417
  f419: sphere r=2.22mm, area 15.5mm2, adj f0,f417
  f420: plane 4.45x2.22mm, normal (0,1,0), area 2.1mm2, adj f0,f421,f422
  f421: sphere r=1.91mm, area 11.4mm2, adj f42,f420
  f422: sphere r=2.22mm, area 15.5mm2, adj f0,f420
  f423: plane 4.45x2.22mm, normal (0,1,0), area 2.1mm2, adj f0,f424,f425
  f424: sphere r=1.91mm, area 11.4mm2, adj f48,f423
  f425: sphere r=2.22mm, area 15.5mm2, adj f0,f423
  f426: plane 4.45x2.22mm, normal (0,1,0), area 2.1mm2, adj f0,f427,f428
  f427: sphere r=1.91mm, area 11.4mm2, adj f46,f426
  f428: sphere r=2.22mm, area 15.5mm2, adj f0,f426
  f429: plane 4.45x2.22mm, normal (0,1,0), area 2.1mm2, adj f0,f430,f431
  f430: sphere r=1.91mm, area 11.4mm2, adj f20,f429
  f431: sphere r=2.22mm, area 15.5mm2, adj f0,f429
  f432: plane 4.45x2.22mm, normal (0,1,0), area 2.1mm2, adj f0,f433,f434
  f433: sphere r=1.91mm, area 11.4mm2, adj f34,f432
  f434: sphere r=2.22mm, area 15.5mm2, adj f0,f432
  f435: plane 4.45x2.22mm, normal (0,1,0), area 2.1mm2, adj f0,f436,f437
  f436: sphere r=1.91mm, area 11.4mm2, adj f56,f435
  f437: sphere r=2.22mm, area 15.5mm2, adj f0,f435
  f438: plane 4.45x2.22mm, normal (0,1,0), area 2.1mm2, adj f0,f439,f440
  f439: sphere r=1.91mm, area 11.4mm2, adj f78,f438
  f440: sphere r=2.22mm, area 15.5mm2, adj f0,f438
  f441: plane 4.45x2.22mm, normal (0,1,0), area 2.1mm2, adj f0,f442,f443
  f442: sphere r=1.91mm, area 11.4mm2, adj f84,f441
  f443: sphere r=2.22mm, area 15.5mm2, adj f0,f441
  f444: plane 4.45x2.22mm, normal (0,1,0), area 2.1mm2, adj f0,f445,f446
  f445: sphere r=1.91mm, area 11.4mm2, adj f63,f444
  f446: sphere r=2.22mm, area 15.5mm2, adj f0,f444
  f447: plane 4.45x2.22mm, normal (0,1,0), area 2.1mm2, adj f0,f448,f449
  f448: sphere r=1.91mm, area 11.4mm2, adj f74,f447
  f449: sphere r=2.22mm, area 15.5mm2, adj f0,f447
  f450: plane 4.45x2.22mm, normal (0,1,0), area 2.1mm2, adj f0,f451,f452
  f451: sphere r=1.91mm, area 11.4mm2, adj f114,f450
  f452: sphere r=2.22mm, area 15.5mm2, adj f0,f450
  f453: plane 4.45x2.22mm, normal (0,1,0), area 2.1mm2, adj f0,f454,f455
  f454: sphere r=1.91mm, area 11.4mm2, adj f120,f453
  f455: sphere r=2.22mm, area 15.5mm2, adj f0,f453
  f456: plane 4.45x2.22mm, normal (0,1,0), area 2.1mm2, adj f0,f457,f458
  f457: sphere r=1.91mm, area 11.4mm2, adj f116,f456
  f458: sphere r=2.22mm, area 15.5mm2, adj f0,f456
  f459: plane 4.45x2.22mm, normal (0,1,0), area 2.1mm2, adj f0,f460,f461
  f460: sphere r=1.91mm, area 11.4mm2, adj f94,f459
  f461: sphere r=2.22mm, area 15.5mm2, adj f0,f459
PLACE A t=(-33.49,-17.15,20.35)mm
PLACE B t=(-39.57,0.6,2.96)mm fixed
MATE planar B.f0 <-> A.f0  axis (0,0,1) through (-39.57,0.53,5.5)mm
